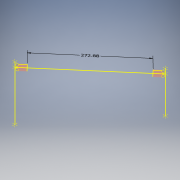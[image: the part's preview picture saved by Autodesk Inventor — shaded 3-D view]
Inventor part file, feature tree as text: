
AUTODESK INVENTOR PART (.ipt)
format: ipt  version: 2018 (Build 220112000, 112)  size: 222,208 bytes
history: native  units: mm
features: other x7, sketch x4, plane x2, extrude x2, boolean_combine x2, delete_face x2, surface_op x2, projected_geometry x1
ambient origin geometry x8: Origin, YZ Plane, XZ Plane, XY Plane, X Axis, Y Axis, Z Axis, Center Point
bodies: Solid3 (feature_tree), Solid4 (feature_tree), Solid1 (feature_tree)
feature tree (22):
  other  "LowerCage.ipt"
  other  "Annotations"
  plane  "Work Plane6"
  plane  "Work Plane8"
  extrude  "Extrusion2"  Depth=10.0mm TaperAngle=0.0deg
  extrude  "Extrusion3"  TaperAngle=0.0deg  [1 undecoded]
  boolean_combine  "Combine3"
  boolean_combine  "Combine4"
  delete_face  "Delete Face3"
  delete_face  "Delete Face4"
  sketch  "Sketch9"  dims[d26=0.0mm d27=0.0mm d28=0.0mm d29=1.0mm d30=1.0mm d31=272.877878mm]
  surface_op  "Trim5"
  surface_op  "Trim6"
  other  "Solid1::LowerCage.ipt"
  other  "TaggingFeature1"
  sketch  "3D Sketch1"
  sketch  "Sketch7"  dims[d0=10.0mm d21=26.75mm d22=0.0mm]
  sketch  "Sketch8"  dims[d23=26.75mm d24=0.0mm d25=0.0mm]
  projected_geometry  "Projected Loop1"
  other  "OffsetSrf3"
  other  "OffsetSrf4"
  other  "Linear Dimension 1"
note: 1 required parameter value undecoded (feature->parameter linkage not recoverable at this tier; creation-order binding heuristic only, values carry confidence <= 0.55)
